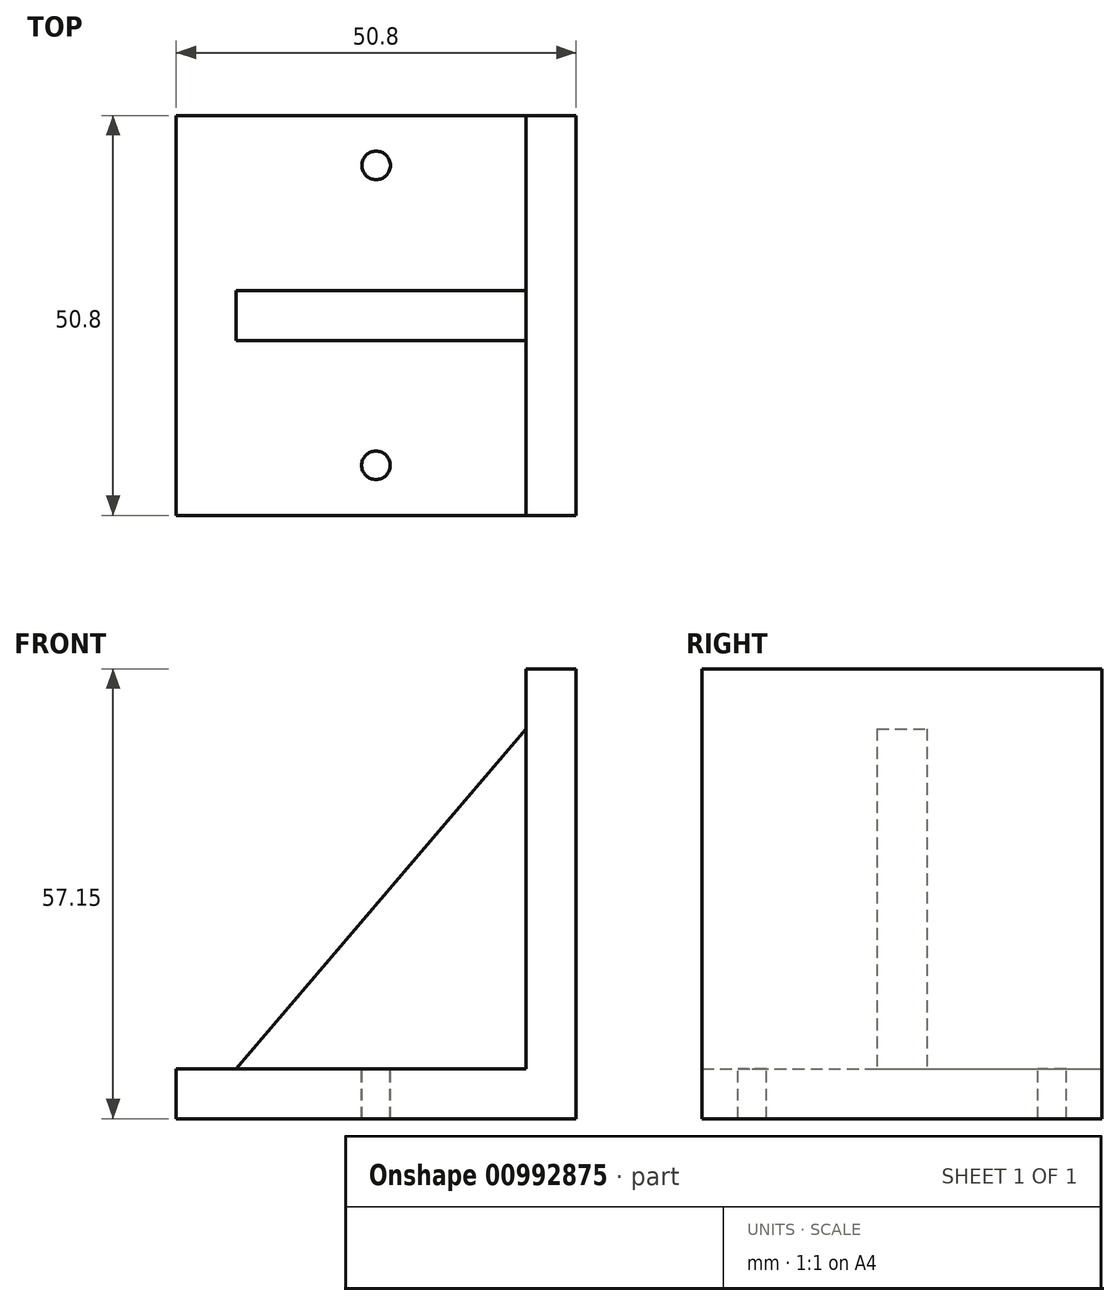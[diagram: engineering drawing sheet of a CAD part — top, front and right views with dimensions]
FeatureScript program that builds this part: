
annotation { "Feature Type Name" : "Feature", "Feature Type Description" : "" }
export const myFeature = defineFeature(function(context is Context, id is Id, definition is map)
    precondition{}
    {
        {
            var Q0;
            Q0=qCreatedBy(makeId("Front.planeOp"),FACE);
            var sketch = newSketch(context, id + "F0", { "sketchPlane" : qUnion([Q0])});
            skLineSegment(sketch, "E0.bottom", {"start": v(-46.48, 19.95) * mm, "end": v(4.32, 19.95) * mm});
            skLineSegment(sketch, "E0.top", {"start": v(-46.48, 13.6) * mm, "end": v(4.32, 13.6) * mm});
            skLineSegment(sketch, "E0.left", {"start": v(-46.48, 19.95) * mm, "end": v(-46.48, 13.6) * mm});
            skLineSegment(sketch, "E0.right", {"start": v(4.32, 19.95) * mm, "end": v(4.32, 13.6) * mm});
            skLineSegment(sketch, "E1.bottom", {"start": v(-2.03, 70.75) * mm, "end": v(4.32, 70.75) * mm});
            skLineSegment(sketch, "E1.top", {"start": v(-2.03, 19.95) * mm, "end": v(4.32, 19.95) * mm});
            skLineSegment(sketch, "E1.left", {"start": v(-2.03, 70.75) * mm, "end": v(-2.03, 19.95) * mm});
            skLineSegment(sketch, "E1.right", {"start": v(4.32, 70.75) * mm, "end": v(4.32, 19.95) * mm});
            skLineSegment(sketch, "E2", {"start": v(-2.03, 63.13) * mm, "end": v(-38.86, 19.95) * mm});
            skSolve(sketch);
        }
        {
            var Q0;
            Q0=makeQuery(id+"F0.imprint","IMPRINT",FACE,{"disambiguationData":[TD([[makeQuery(id+"F0.imprint","IMPRINT",EDGE,{"derivedFrom":sQuery(id+"F0.wireOp",EDGE,"E0.top")}),1.0]])]});
            var Q1;
            {var subQ3=sQuery(id+"F0.wireOp",EDGE,"E1.bottom");Q1=makeQuery(id+"F0.imprint","IMPRINT",FACE,{"disambiguationData":[TD([[makeQuery(id+"F0.imprint","IMPRINT",EDGE,{"derivedFrom":subQ3}),-1.0]])]});}
            extrude(context, id + "F1", {"entities" : qUnion([Q0, Q1]), "endBound" : BoundingType.SYMMETRIC, "depth" : 50.8 * mm, "offsetDistance" : 25.4 * mm});
        }
        {
            var Q0;
            Q0 = qSketchRegion(id + "F0", true);
            extrude(context, id + "F2", {"entities" : qUnion([Q0]), "operationType" : NewBodyOperationType.ADD, "endBound" : BoundingType.SYMMETRIC, "depth" : 6.35 * mm, "offsetDistance" : 25.4 * mm});
        }
        {
            var Q0;
            Q0=makeQuery(id+"F1.opExtrude","SWEPT_FACE",FACE,{"disambiguationData":[OSD([sQuery(id+"F0.wireOp",EDGE,"E0.bottom")])]});
            var sketch = newSketch(context, id + "F3", { "sketchPlane" : qUnion([Q0])});
            skCircle(sketch, "E3", {"center": v(-21.08, 19.05) * mm, "radius": 1.81 * mm});
            skCircle(sketch, "E4.1.0.0", {"center": v(-21.12, -19.05) * mm, "radius": 1.81 * mm});
            skLineSegment(sketch, "E4.direction1", {"start": v(-21.08, 19.05) * mm, "end": v(-21.12, -19.05) * mm, "construction": true});
            skSolve(sketch);
        }
        {
            var Q0;
            Q0=makeQuery(id+"F3.imprint","IMPRINT",FACE,{"disambiguationData":[TD([[makeQuery(id+"F3.imprint","IMPRINT",EDGE,{"derivedFrom":sQuery(id+"F3.wireOp",EDGE,"E3")}),1.0]])]});
            var Q1;
            Q1=makeQuery(id+"F3.imprint","IMPRINT",FACE,{"disambiguationData":[TD([[makeQuery(id+"F3.imprint","IMPRINT",EDGE,{"derivedFrom":sQuery(id+"F3.wireOp",EDGE,"E4.1.0.0")}),1.0]])]});
            var Q2;
            Q2=sQuery(id+"F3.wireOp",EDGE,"E3");
            var Q3;
            Q3=sQuery(id+"F3.wireOp",EDGE,"E4.1.0.0");
            extrude(context, id + "F4", {"entities" : qUnion([Q0, Q1]), "operationType" : NewBodyOperationType.REMOVE, "surfaceEntities" : qUnion([Q2, Q3]), "oppositeDirection" : true, "depth" : 25.4 * mm, "offsetDistance" : 25.4 * mm});
        }
    });
